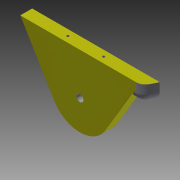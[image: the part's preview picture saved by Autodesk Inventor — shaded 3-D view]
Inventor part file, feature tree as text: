
AUTODESK INVENTOR PART (.ipt)
format: ipt  version: 2015 (Build 190159000, 159)  size: 137,216 bytes
history: native  units: mm
features: extrude x5, sketch x5, fillet x1
ambient origin geometry x8: Origin, YZ Plane, XZ Plane, XY Plane, X Axis, Y Axis, Z Axis, Center Point
bodies: Solid1 (feature_tree)
feature tree (11):
  extrude  "Extrusion1"  Depth=50.0mm
  extrude  "Extrusion2"  Depth=6.0mm
  extrude  "Extrusion3"  Depth=10.0mm
  extrude  "Extrusion4"  Depth=10.0mm TaperAngle=0.0deg
  extrude  "Extrusion5"  Depth=10.0mm
  fillet  "Fillet1"  Radius=10.0mm
  sketch  "Sketch1"  dims[d4=50.0mm d5=50.0mm]
  sketch  "Sketch2"  dims[d6=100.0mm d7=6.0mm]
  sketch  "Sketch3"  dims[d8=10.0mm d9=0.0mm d11=2.0mm]
  sketch  "Sketch4"  dims[d12=2.0mm d13=10.0mm d14=0.0mm]
  sketch  "Sketch5"  dims[d15=15.0mm d16=10.0mm d17=10.0mm d18=0.0mm d19=6.4mm d20=0.0mm d21=48.5mm d22=90.0deg d24=15.0mm d25=0.0mm d26=8.0mm]
